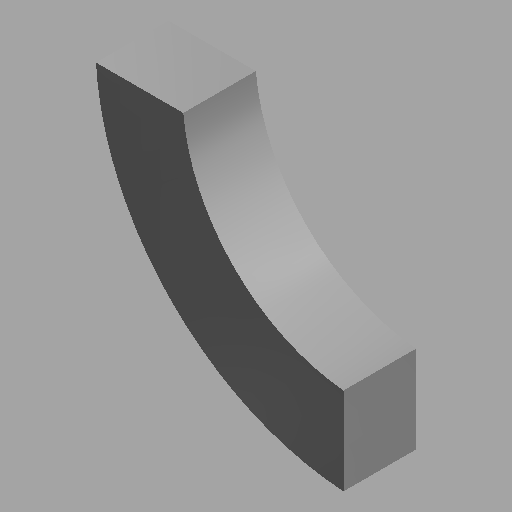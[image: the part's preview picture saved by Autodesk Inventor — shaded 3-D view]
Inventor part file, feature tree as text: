
AUTODESK INVENTOR PART (.ipt)
format: ipt  version: 2023 (Build 270158030, 158C)  size: 93,696 bytes
history: native  units: mm (DEFAULTED — no unit token found)
features: other x1, direct_edit x1, revolve x1
ambient origin geometry x8: Origin, YZ Plane, XZ Plane, XY Plane, X Axis, Y Axis, Z Axis, Center Point
bodies: Solid1 (feature_tree)
feature tree (3):
  other  "Arch header 3 (C)"
  direct_edit  "Direct Edit1"
  revolve  "Rotate1"  [1 undecoded]
note: 1 required parameter value undecoded (feature->parameter linkage not recoverable at this tier; creation-order binding heuristic only, values carry confidence <= 0.55)
